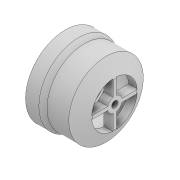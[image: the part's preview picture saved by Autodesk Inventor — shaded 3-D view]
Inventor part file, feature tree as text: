
AUTODESK INVENTOR PART (.ipt)
format: ipt  version: 2020 (Build 240168000, 168)  size: 722,432 bytes
history: native  units: mm
features: sketch x9, projected_geometry x5, revolve x4, extrude x4, plane x2, thread x1, helix x1
ambient origin geometry x8: Origin, YZ Plane, XZ Plane, XY Plane, X Axis, Y Axis, Z Axis, Center Point
bodies: Solid1 (feature_tree), Solid2 (feature_tree)
feature tree (26):
  revolve  "Revolution1"  [1 undecoded]
  thread  "Thread1"  [1 undecoded]
  revolve  "Revolution2"  [1 undecoded]
  helix  "Coil1"  [1 undecoded]
  plane  "Work Plane1"
  extrude  "Extrusion1"  Depth=17.95mm
  extrude  "Extrusion2"  Depth=16.0mm
  plane  "Work Plane2"
  revolve  "Revolution4"  [1 undecoded]
  extrude  "Extrusion7"  TaperAngle=0.0deg  [1 undecoded]
  extrude  "Extrusion8"  Depth=21.8mm
  revolve  "Revolution5"  [1 undecoded]
  sketch  "Sketch1"  dims[d0=25.0mm d1=11.0mm d2=11.25mm]
  sketch  "Sketch2"  dims[d3=9.0mm d10=20.5mm d12=120.0deg]
  sketch  "Sketch3"  dims[d13=0.0mm d14=17.95mm]
  sketch  "Sketch4"  dims[d15=17.95mm d16=16.0mm]
  sketch  "Sketch5"  dims[d17=17.0mm d18=20.5mm]
  sketch  "Sketch11"  dims[d19=12.0mm d20=0.0mm]
  projected_geometry  "Projected Loop1"
  sketch  "Sketch12"  dims[d21=20.0mm d23=21.8mm]
  projected_geometry  "Projected Loop2"
  sketch  "Sketch13"  dims[d24=3.0mm d25=10.5mm]
  projected_geometry  "Projected Loop3"
  projected_geometry  "Projected Loop4"
  sketch  "Sketch14"  dims[d26=0.0mm d27=90.0deg d28=2.0mm d29=2.0mm d30=2.0mm d31=7.0mm d32=1.5mm d33=9.599311mm d34=0.240125mm d35=0.240125mm d38=1.5mm d40=9.599311mm d42=0.0mm d43=1.5015mm d44=10.0mm d45=10.0mm d46=0.0mm d47=0.0mm d48=0.0mm d49=0.0mm d50=0.0mm d51=-15.164mm d52=3.5mm d53=8.0mm d54=2.0mm d55=2.0mm d56=3.0mm d57=0.0mm d58=6.5mm d59=2.0mm d60=0.0mm d61=20.5mm d88=90.0deg d89=90.0deg d90=0.0mm d91=0.0mm d92=10.0mm d93=0.0mm d94=90.0deg]
  projected_geometry  "Projected Loop5"
note: 7 required parameter values undecoded (feature->parameter linkage not recoverable at this tier; creation-order binding heuristic only, values carry confidence <= 0.55)